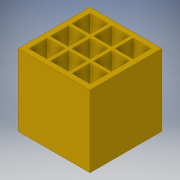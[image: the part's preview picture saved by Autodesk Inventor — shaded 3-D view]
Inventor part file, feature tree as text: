
AUTODESK INVENTOR PART (.ipt)
format: ipt  version: 2019 (Build 230136000, 136)  size: 144,896 bytes
history: native  units: in
note: dims shown in document units (in); Inventor stores cm internally (conversion verified against a paired STEP export)
features: extrude x2, sketch x2, projected_geometry x1
ambient origin geometry x8: Origin, YZ Plane, XZ Plane, XY Plane, X Axis, Y Axis, Z Axis, Center Point
bodies: Solid1 (feature_tree)
feature tree (5):
  extrude  "Extrusion1"  Depth=2.0in
  extrude  "Extrusion2"  Depth=0.5in
  sketch  "Sketch1"  dims[d0=2.0in d1=2.0in]
  sketch  "Sketch2"  dims[d2=2.0in d3=0.0in d4=0.5in d5=0.5in d6=0.15in d7=0.15in d8=1.1811in d10=0.6in d11=1.1811in d13=0.6in d16=1.0in d17=0.0in]
  projected_geometry  "Projected Loop1"
